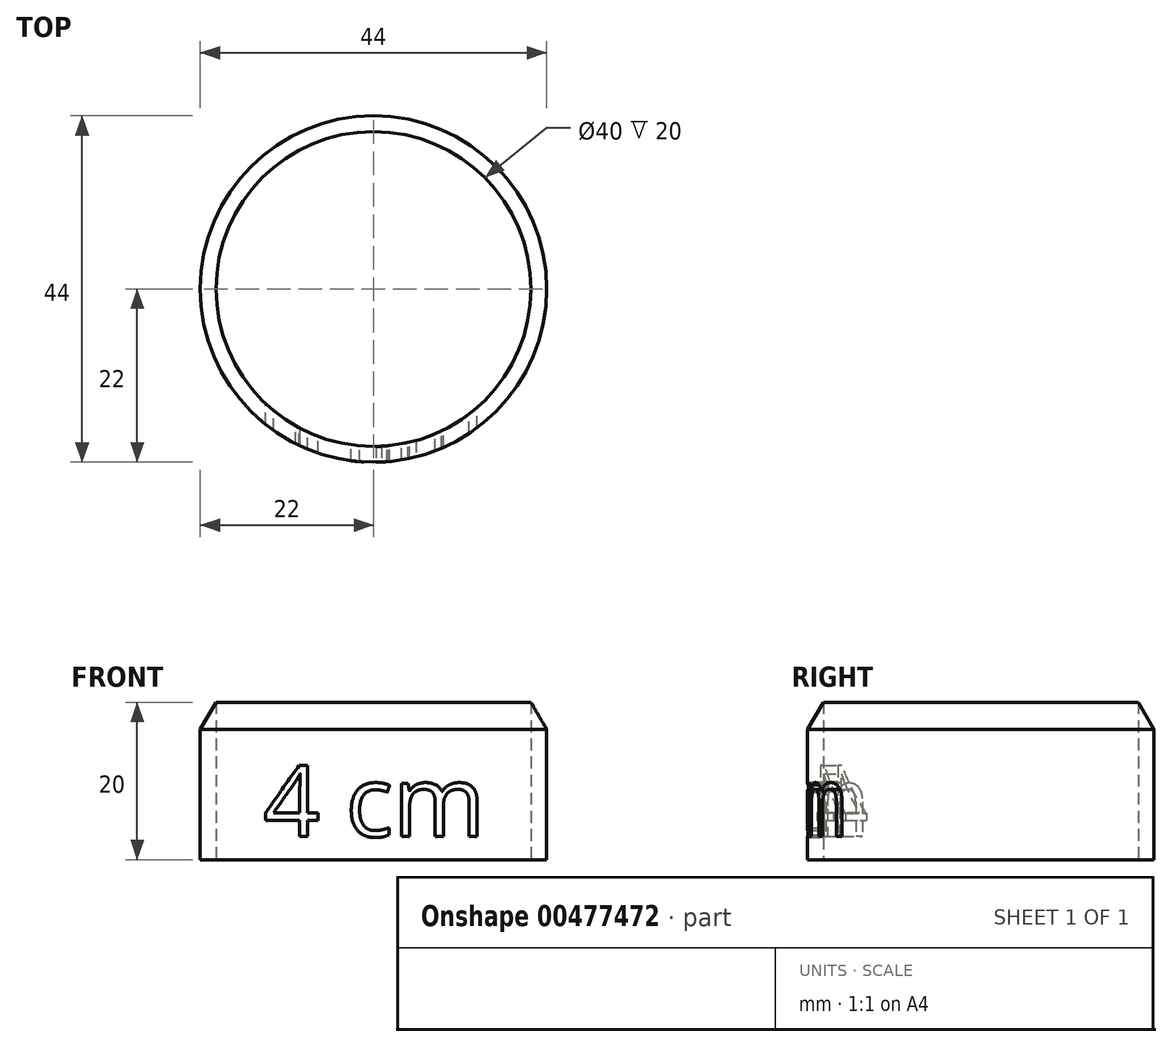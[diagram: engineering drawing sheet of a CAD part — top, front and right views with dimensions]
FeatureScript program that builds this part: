
annotation { "Feature Type Name" : "Feature", "Feature Type Description" : "" }
export const myFeature = defineFeature(function(context is Context, id is Id, definition is map)
    precondition{}
    {
        {
            var Q0;
            Q0=qCreatedBy(makeId("Top.planeOp"),FACE);
            var sketch = newSketch(context, id + "F0", { "sketchPlane" : qUnion([Q0])});
            skCircle(sketch, "E0", {"center": v(0, 0) * mm, "radius": 20 * mm});
            skCircle(sketch, "E1", {"center": v(0, 0) * mm, "radius": 22 * mm});
            skSolve(sketch);
        }
        {
            var Q0;
            Q0=makeQuery(id+"F0.imprint","IMPRINT",FACE,{"disambiguationData":[TD([[makeQuery(id+"F0.imprint","IMPRINT",EDGE,{"derivedFrom":sQuery(id+"F0.wireOp",EDGE,"E0")}),-1.0]])]});
            extrude(context, id + "F1", {"entities" : qUnion([Q0]), "depth" : 20 * mm});
        }
        {
            var Q0;
            Q0=qCreatedBy(makeId("Front.planeOp"),FACE);
            var sketch = newSketch(context, id + "F2", { "sketchPlane" : qUnion([Q0])});
            skText(sketch, "E2", { "text": "4 cm", "fontName": "OpenSans-Regular.ttf"});
            const initialGuessF2  = {"E2": [-0.014, 0.00293, 1, 0, 0.00907]};
            skSetInitialGuess(sketch, initialGuessF2);
            skSolve(sketch);
        }
        {
            var Q0;
            Q0 = qSketchRegion(id + "F2", true);
            var Q1;
            Q1=makeQuery(id+"F1.opExtrude","SWEPT_FACE",FACE,{"disambiguationData":[OSD([sQuery(id+"F0.wireOp",EDGE,"E1")])]});
            extrude(context, id + "F3", {"entities" : qUnion([Q0]), "operationType" : NewBodyOperationType.REMOVE, "endBound" : BoundingType.UP_TO_SURFACE, "endBoundEntityFace" : qUnion([Q1]), "depth" : 25 * mm});
        }
        {
            var Q0;
            Q0=makeQuery(id+"F1.opExtrude","CAP_EDGE",EDGE,{"disambiguationData":[OSD([sQuery(id+"F0.wireOp",EDGE,"E1")])],"isStart":false});
            chamfer(context, id + "F4", {"entities" : qUnion([Q0]), "chamferType" : ChamferType.OFFSET_ANGLE, "width" : 2 * mm, "oppositeDirection" : false, "angle" : 60 * degree, "tangentPropagation" : true});
        }
    });
